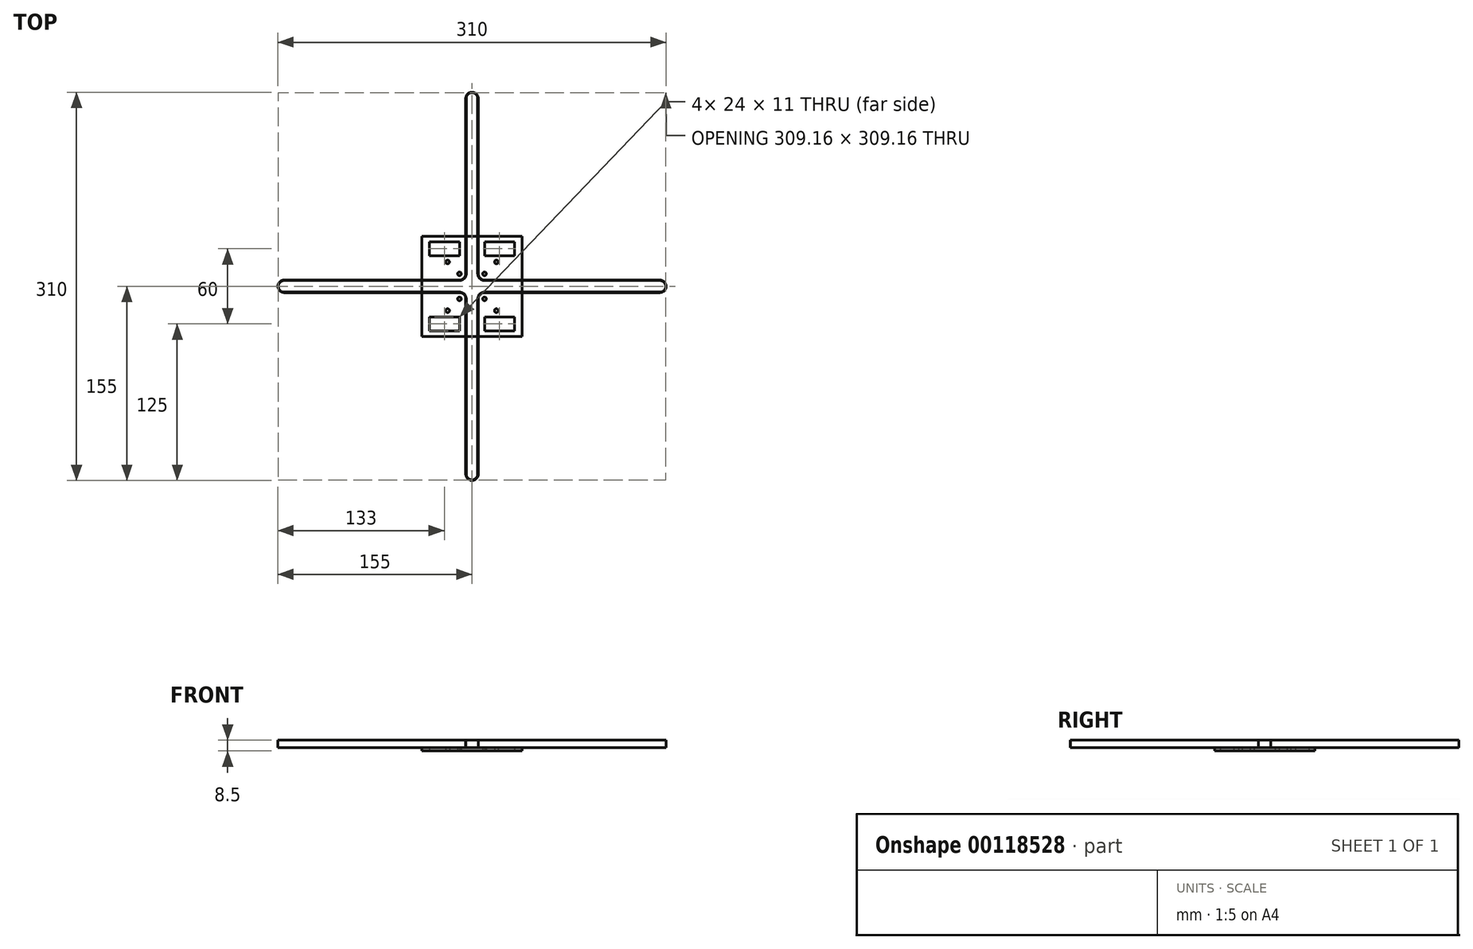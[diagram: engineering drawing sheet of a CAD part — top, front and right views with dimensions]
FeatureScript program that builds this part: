
annotation { "Feature Type Name" : "Feature", "Feature Type Description" : "" }
export const myFeature = defineFeature(function(context is Context, id is Id, definition is map)
    precondition{}
    {
        {
            var Q0;
            Q0=qCreatedBy(makeId("Top.planeOp"),FACE);
            var sketch = newSketch(context, id + "F0", { "sketchPlane" : qUnion([Q0])});
            skLineSegment(sketch, "E0", {"start": v(-126.92, 30) * mm, "end": v(134.24, 30) * mm, "construction": true});
            skLineSegment(sketch, "E1", {"start": v(-126.68, -30) * mm, "end": v(132.4, -30) * mm, "construction": true});
            skLineSegment(sketch, "E2", {"start": v(-22, 80.91) * mm, "end": v(-22, -74.2) * mm, "construction": true});
            skLineSegment(sketch, "E3", {"start": v(22, 83.6) * mm, "end": v(22, -72.05) * mm, "construction": true});
            skLineSegment(sketch, "E4.bottom", {"start": v(-40, 40) * mm, "end": v(40, 40) * mm});
            skLineSegment(sketch, "E4.top", {"start": v(-40, -40) * mm, "end": v(40, -40) * mm});
            skLineSegment(sketch, "E4.left", {"start": v(-40, 40) * mm, "end": v(-40, -40) * mm});
            skLineSegment(sketch, "E4.right", {"start": v(40, 40) * mm, "end": v(40, -40) * mm});
            skPoint(sketch, "E4.middle", {"position": v(0, 0) * mm});
            skLineSegment(sketch, "E5.bottom", {"start": v(-34, 35.5) * mm, "end": v(-10, 35.5) * mm});
            skLineSegment(sketch, "E5.top", {"start": v(-34, 24.5) * mm, "end": v(-10, 24.5) * mm});
            skLineSegment(sketch, "E5.left", {"start": v(-34, 35.5) * mm, "end": v(-34, 24.5) * mm});
            skLineSegment(sketch, "E5.right", {"start": v(-10, 35.5) * mm, "end": v(-10, 24.5) * mm});
            skPoint(sketch, "E5.middle", {"position": v(-22, 30) * mm});
            skLineSegment(sketch, "E6.bottom", {"start": v(10, 35.5) * mm, "end": v(34, 35.5) * mm});
            skLineSegment(sketch, "E6.top", {"start": v(10, 24.5) * mm, "end": v(34, 24.5) * mm});
            skLineSegment(sketch, "E6.left", {"start": v(10, 35.5) * mm, "end": v(10, 24.5) * mm});
            skLineSegment(sketch, "E6.right", {"start": v(34, 35.5) * mm, "end": v(34, 24.5) * mm});
            skPoint(sketch, "E6.middle", {"position": v(22, 30) * mm});
            skLineSegment(sketch, "E7.bottom", {"start": v(-34, -24.5) * mm, "end": v(-10, -24.5) * mm});
            skLineSegment(sketch, "E7.top", {"start": v(-34, -35.5) * mm, "end": v(-10, -35.5) * mm});
            skLineSegment(sketch, "E7.left", {"start": v(-34, -24.5) * mm, "end": v(-34, -35.5) * mm});
            skLineSegment(sketch, "E7.right", {"start": v(-10, -24.5) * mm, "end": v(-10, -35.5) * mm});
            skPoint(sketch, "E7.middle", {"position": v(-22, -30) * mm});
            skLineSegment(sketch, "E8.bottom", {"start": v(10, -24.5) * mm, "end": v(34, -24.5) * mm});
            skLineSegment(sketch, "E8.top", {"start": v(10, -35.5) * mm, "end": v(34, -35.5) * mm});
            skLineSegment(sketch, "E8.left", {"start": v(10, -24.5) * mm, "end": v(10, -35.5) * mm});
            skLineSegment(sketch, "E8.right", {"start": v(34, -24.5) * mm, "end": v(34, -35.5) * mm});
            skPoint(sketch, "E8.middle", {"position": v(22, -30) * mm});
            skLineSegment(sketch, "E9.bottom", {"start": v(-10, 10) * mm, "end": v(10, 10) * mm, "construction": true});
            skLineSegment(sketch, "E9.top", {"start": v(-10, -10) * mm, "end": v(10, -10) * mm, "construction": true});
            skLineSegment(sketch, "E9.left", {"start": v(-10, 10) * mm, "end": v(-10, -10) * mm, "construction": true});
            skLineSegment(sketch, "E9.right", {"start": v(10, 10) * mm, "end": v(10, -10) * mm, "construction": true});
            skCircle(sketch, "E10", {"center": v(-10, 10) * mm, "radius": 1.5 * mm});
            skCircle(sketch, "E11", {"center": v(10, 10) * mm, "radius": 1.5 * mm});
            skCircle(sketch, "E12", {"center": v(-10, -10) * mm, "radius": 1.5 * mm});
            skCircle(sketch, "E13", {"center": v(10, -10) * mm, "radius": 1.5 * mm});
            skCircle(sketch, "E14", {"center": v(-10, 10) * mm, "radius": 5.75 * mm, "construction": true});
            skLineSegment(sketch, "E15", {"start": v(40, 40) * mm, "end": v(-40, -40) * mm, "construction": true});
            skLineSegment(sketch, "E16", {"start": v(-40, 40) * mm, "end": v(40, -40) * mm, "construction": true});
            skCircle(sketch, "E17", {"center": v(0, 0) * mm, "radius": 27.5 * mm, "construction": true});
            skCircle(sketch, "E18", {"center": v(19.44, 19.44) * mm, "radius": 1.5 * mm});
            skCircle(sketch, "E19", {"center": v(-19.44, 19.44) * mm, "radius": 1.5 * mm});
            skCircle(sketch, "E20", {"center": v(-19.44, -19.44) * mm, "radius": 1.5 * mm});
            skCircle(sketch, "E21", {"center": v(19.44, -19.44) * mm, "radius": 1.5 * mm});
            skSolve(sketch);
        }
        {
            var Q0;
            Q0=qSketchRegion(id+"F0",true);
            extrude(context, id + "F1", {"entities" : qUnion([Q0]), "depth" : 2.5 * mm});
        }
        {
            var Q0;
            Q0=makeQuery(id+"F1.opExtrude","CAP_FACE",FACE,{"disambiguationData":[OSD([sQuery(id+"F0.wireOp",EDGE,"E4.bottom"),sQuery(id+"F0.wireOp",EDGE,"E4.top"),sQuery(id+"F0.wireOp",EDGE,"E4.left"),sQuery(id+"F0.wireOp",EDGE,"E4.right"),sQuery(id+"F0.wireOp",EDGE,"E5.bottom"),sQuery(id+"F0.wireOp",EDGE,"E5.top"),sQuery(id+"F0.wireOp",EDGE,"E5.left"),sQuery(id+"F0.wireOp",EDGE,"E5.right"),sQuery(id+"F0.wireOp",EDGE,"E6.bottom"),sQuery(id+"F0.wireOp",EDGE,"E6.top"),sQuery(id+"F0.wireOp",EDGE,"E6.left"),sQuery(id+"F0.wireOp",EDGE,"E6.right"),sQuery(id+"F0.wireOp",EDGE,"E7.bottom"),sQuery(id+"F0.wireOp",EDGE,"E7.top"),sQuery(id+"F0.wireOp",EDGE,"E7.left"),sQuery(id+"F0.wireOp",EDGE,"E7.right"),sQuery(id+"F0.wireOp",EDGE,"E8.bottom"),sQuery(id+"F0.wireOp",EDGE,"E8.top"),sQuery(id+"F0.wireOp",EDGE,"E8.left"),sQuery(id+"F0.wireOp",EDGE,"E8.right"),sQuery(id+"F0.wireOp",EDGE,"E10"),sQuery(id+"F0.wireOp",EDGE,"E11"),sQuery(id+"F0.wireOp",EDGE,"E12"),sQuery(id+"F0.wireOp",EDGE,"E13")])],"isStart":false});
            var sketch = newSketch(context, id + "F2", { "sketchPlane" : qUnion([Q0])});
            skLineSegment(sketch, "E22", {"start": v(-199.3, 0) * mm, "end": v(227.96, 0) * mm, "construction": true});
            skLineSegment(sketch, "E23", {"start": v(0, 183.41) * mm, "end": v(0, -159.24) * mm, "construction": true});
            skArc(sketch, "E24", {"start": v(-150, 5) * mm, "mid": v(-155, 0) * mm, "end": v(-150, -5) * mm});
            skArc(sketch, "E25", {"start": v(150, -5) * mm, "mid": v(155, 0) * mm, "end": v(150, 5) * mm});
            skArc(sketch, "E26", {"start": v(5, 150) * mm, "mid": v(0, 155) * mm, "end": v(-5, 150) * mm});
            skArc(sketch, "E27", {"start": v(-5, -150) * mm, "mid": v(0, -155) * mm, "end": v(5, -150) * mm});
            skLineSegment(sketch, "E28", {"start": v(-150, 5) * mm, "end": v(-10, 5) * mm});
            skLineSegment(sketch, "E29", {"start": v(-150, -5) * mm, "end": v(-10, -5) * mm});
            skLineSegment(sketch, "E30", {"start": v(10, 5) * mm, "end": v(150, 5) * mm});
            skLineSegment(sketch, "E31", {"start": v(10, -5) * mm, "end": v(150, -5) * mm});
            skLineSegment(sketch, "E32", {"start": v(-5, 150) * mm, "end": v(-5, 10) * mm});
            skLineSegment(sketch, "E33", {"start": v(5, 150) * mm, "end": v(5, 10) * mm});
            skLineSegment(sketch, "E34", {"start": v(-5, -150) * mm, "end": v(-5, -10) * mm});
            skLineSegment(sketch, "E35", {"start": v(5, -150) * mm, "end": v(5, -10) * mm});
            skArc(sketch, "E36", {"start": v(-5, 10) * mm, "mid": v(-6.46, 6.46) * mm, "end": v(-10, 5) * mm});
            skArc(sketch, "E37", {"start": v(10, 5) * mm, "mid": v(6.46, 6.46) * mm, "end": v(5, 10) * mm});
            skArc(sketch, "E38", {"start": v(5, -10) * mm, "mid": v(6.46, -6.46) * mm, "end": v(10, -5) * mm});
            skArc(sketch, "E39", {"start": v(-10, -5) * mm, "mid": v(-6.46, -6.46) * mm, "end": v(-5, -10) * mm});
            skArc(sketch, "E40.0", {"start": v(-150, 4.58) * mm, "mid": v(-154.58, 0) * mm, "end": v(-150, -4.58) * mm});
            skLineSegment(sketch, "E40.1", {"start": v(-150, 4.58) * mm, "end": v(-10, 4.58) * mm});
            skArc(sketch, "E40.2", {"start": v(-4.58, 10) * mm, "mid": v(-6.17, 6.17) * mm, "end": v(-10, 4.58) * mm});
            skLineSegment(sketch, "E40.3", {"start": v(-4.58, 150) * mm, "end": v(-4.58, 10) * mm});
            skArc(sketch, "E40.4", {"start": v(4.58, 150) * mm, "mid": v(0, 154.58) * mm, "end": v(-4.58, 150) * mm});
            skLineSegment(sketch, "E40.5", {"start": v(4.58, -150) * mm, "end": v(4.58, -10) * mm});
            skArc(sketch, "E40.6", {"start": v(-4.58, -150) * mm, "mid": v(0, -154.58) * mm, "end": v(4.58, -150) * mm});
            skLineSegment(sketch, "E40.7", {"start": v(-4.58, -150) * mm, "end": v(-4.58, -10) * mm});
            skArc(sketch, "E40.8", {"start": v(-10, -4.58) * mm, "mid": v(-6.17, -6.17) * mm, "end": v(-4.58, -10) * mm});
            skArc(sketch, "E40.9", {"start": v(4.58, -10) * mm, "mid": v(6.17, -6.17) * mm, "end": v(10, -4.58) * mm});
            skLineSegment(sketch, "E40.10", {"start": v(10, -4.58) * mm, "end": v(150, -4.58) * mm});
            skArc(sketch, "E40.11", {"start": v(150, -4.58) * mm, "mid": v(154.58, 0) * mm, "end": v(150, 4.58) * mm});
            skLineSegment(sketch, "E40.12", {"start": v(10, 4.58) * mm, "end": v(150, 4.58) * mm});
            skArc(sketch, "E40.13", {"start": v(10, 4.58) * mm, "mid": v(6.17, 6.17) * mm, "end": v(4.58, 10) * mm});
            skLineSegment(sketch, "E40.14", {"start": v(-150, -4.58) * mm, "end": v(-10, -4.58) * mm});
            skLineSegment(sketch, "E40.15", {"start": v(4.58, 150) * mm, "end": v(4.58, 10) * mm});
            skSolve(sketch);
        }
        {
            var Q0;
            Q0=qSketchRegion(id+"F2",true);
            extrude(context, id + "F3", {"entities" : qUnion([Q0]), "depth" : 6 * mm});
        }
    });
